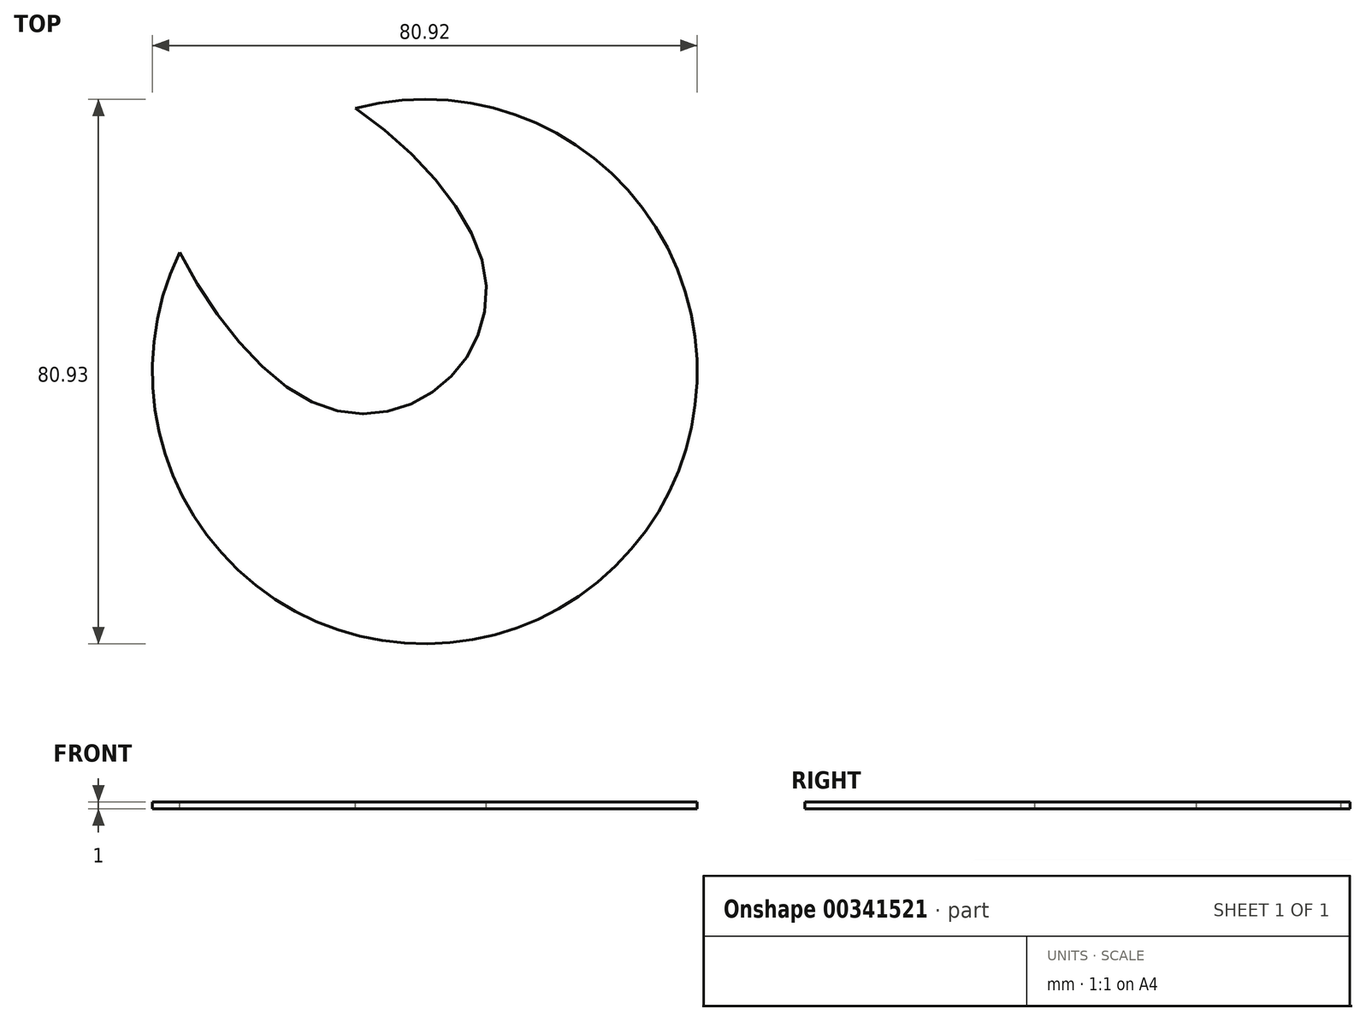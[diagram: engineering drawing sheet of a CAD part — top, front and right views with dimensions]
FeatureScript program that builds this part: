
annotation { "Feature Type Name" : "Feature", "Feature Type Description" : "" }
export const myFeature = defineFeature(function(context is Context, id is Id, definition is map)
    precondition{}
    {
        {
            var Q0;
            Q0=qCreatedBy(makeId("Top.planeOp"),FACE);
            var sketch = newSketch(context, id + "F0", { "sketchPlane" : qUnion([Q0])});
            skCircle(sketch, "E0", {"center": v(39.9, 40.44) * mm, "radius": 40.46 * mm});
            skPoint(sketch, "E0.first.point", {"position": v(0, 47.17) * mm});
            skPoint(sketch, "E0.second.point", {"position": v(0, 33.7) * mm});
            skPoint(sketch, "E0.third.point", {"position": v(38.45, 0) * mm});
            skSolve(sketch);
        }
        {
            var Q0;
            Q0=makeQuery(id+"F0.imprint","IMPRINT",FACE,{"disambiguationData":[TD([[makeQuery(id+"F0.imprint","IMPRINT",EDGE,{"derivedFrom":sQuery(id+"F0.wireOp",EDGE,"E0")}),1.0]])]});
            extrude(context, id + "F1", {"entities" : qUnion([Q0]), "depth" : 1 * mm});
        }
        {
            var Q0;
            Q0=makeQuery(id+"F1.opExtrude","CAP_FACE",FACE,{"disambiguationData":[OSD([sQuery(id+"F0.wireOp",EDGE,"E0")])],"isStart":false});
            var sketch = newSketch(context, id + "F2", { "sketchPlane" : qUnion([Q0])});
            skSolve(sketch);
        }
        {
            var Q0;
            Q0=makeQuery(id+"F2.imprint","IMPRINT",FACE,{"disambiguationData":[TD([[makeQuery(id+"F2.imprint","IMPRINT",EDGE,{"derivedFrom":makeQuery(id+"F1.opExtrude","CAP_EDGE",EDGE,{"disambiguationData":[OSD([sQuery(id+"F0.wireOp",EDGE,"E0")])],"isStart":false})}),1.0]])]});
            var sketch = newSketch(context, id + "F3", { "sketchPlane" : qUnion([Q0])});
            skFitSpline(sketch, "E1", {"points": [v(48.62, 56.15) * mm, v(24.8, 35.22) * mm, v(0, 87.56) * mm, v(48.62, 56.15) * mm]});
            skSolve(sketch);
        }
        {
            var Q0;
            {var subQ0=sQuery(id+"F3.wireOp",EDGE,"E1");var subQ1=makeQuery(id+"F2.imprint","IMPRINT",EDGE,{"derivedFrom":makeQuery(id+"F1.opExtrude","CAP_EDGE",EDGE,{"disambiguationData":[OSD([sQuery(id+"F0.wireOp",EDGE,"E0")])],"isStart":false})});var subQ2=makeQuery(id+"F3.imprint","INTERSECT",VERTEX,{"disambiguationData":[OD(0.0)],"derivedFrom":[subQ1,subQ0]});Q0=makeQuery(id+"F3.imprint","IMPRINT",FACE,{"disambiguationData":[TD([[makeQuery(id+"F3.imprint","IMPRINT",EDGE,{"disambiguationData":[TD([[subQ2,1.0]])],"derivedFrom":subQ0}),-1.0]])]});}
            extrude(context, id + "F4", {"entities" : qUnion([Q0]), "operationType" : NewBodyOperationType.REMOVE, "oppositeDirection" : true, "depth" : 25.4 * mm});
        }
    });
